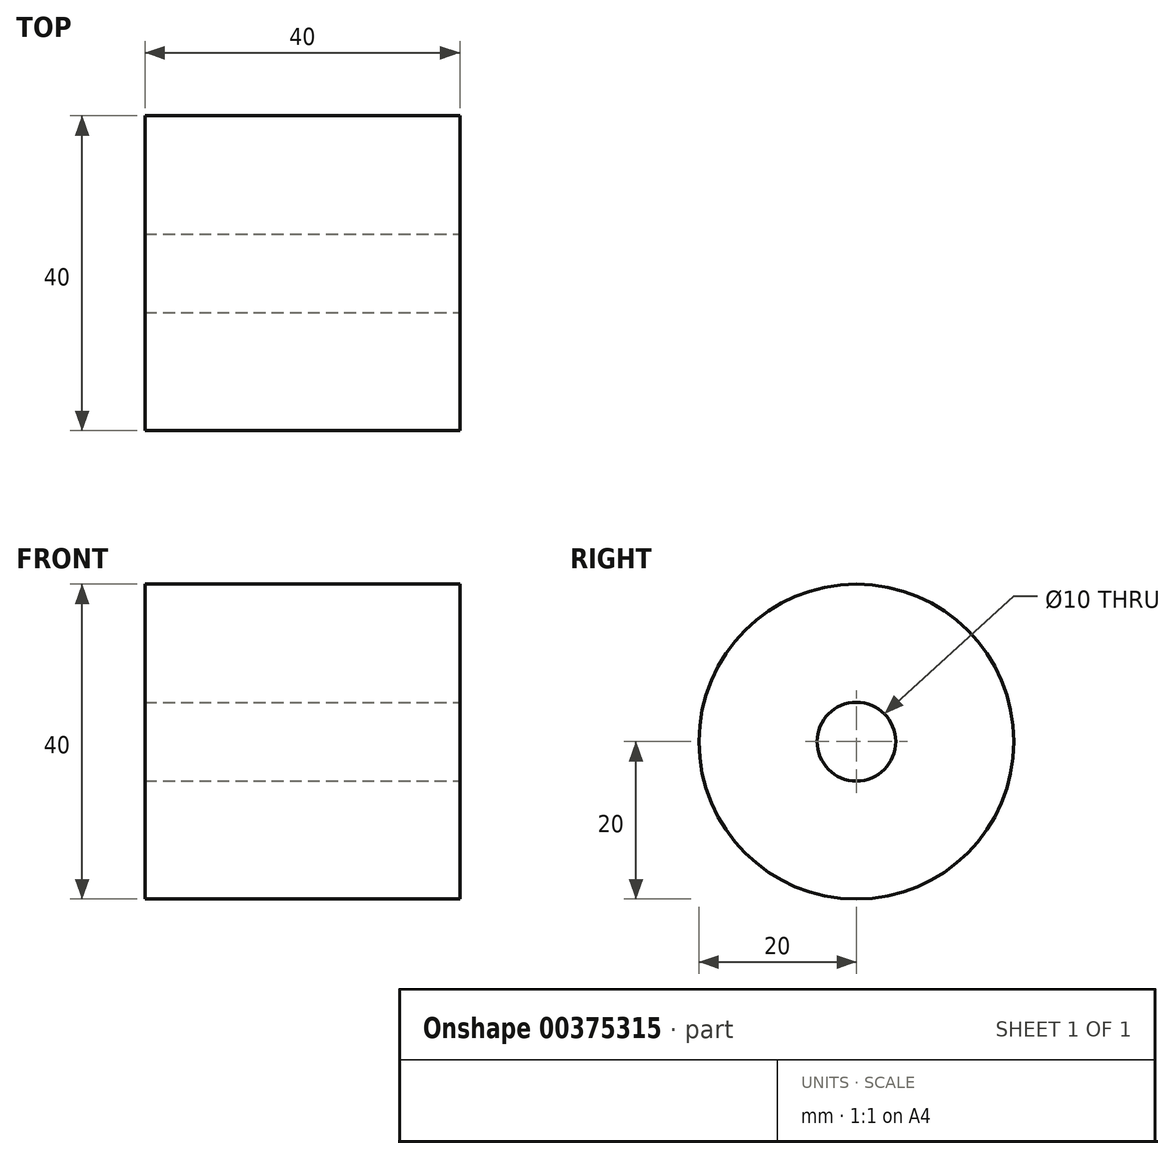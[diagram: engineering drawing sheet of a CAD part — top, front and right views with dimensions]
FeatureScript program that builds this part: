
annotation { "Feature Type Name" : "Feature", "Feature Type Description" : "" }
export const myFeature = defineFeature(function(context is Context, id is Id, definition is map)
    precondition{}
    {
        {
            var Q0;
            Q0=qCreatedBy(makeId("Front.planeOp"),FACE);
            var sketch = newSketch(context, id + "F0", { "sketchPlane" : qUnion([Q0])});
            skLineSegment(sketch, "E0.bottom", {"start": v(-20.03, 20) * mm, "end": v(19.97, 20) * mm});
            skLineSegment(sketch, "E0.top", {"start": v(-20.03, 0) * mm, "end": v(19.97, 0) * mm});
            skLineSegment(sketch, "E0.left", {"start": v(-20.03, 20) * mm, "end": v(-20.03, 0) * mm});
            skLineSegment(sketch, "E0.right", {"start": v(19.97, 20) * mm, "end": v(19.97, 0) * mm});
            skSolve(sketch);
        }
        {
            var Q0;
            Q0 = qSketchRegion(id + "F0", true);
            var Q1;
            Q1=sQuery(id+"F0.wireOp",EDGE,"E0.top");
            revolve(context, id + "F1", {"entities" : qUnion([Q0]), "axis" : qUnion([Q1]), "revolveType" : RevolveType.FULL});
        }
        {
            var Q0;
            Q0=makeQuery(id+"F1.opRevolve","SWEPT_FACE",FACE,{"disambiguationData":[OSD([sQuery(id+"F0.wireOp",EDGE,"E0.right")])]});
            var sketch = newSketch(context, id + "F2", { "sketchPlane" : qUnion([Q0])});
            skCircle(sketch, "E1", {"center": v(0, 0) * mm, "radius": 5 * mm});
            skSolve(sketch);
        }
        {
            var Q0;
            Q0 = qSketchRegion(id + "F2", true);
            extrude(context, id + "F3", {"entities" : qUnion([Q0]), "operationType" : NewBodyOperationType.REMOVE, "endBound" : BoundingType.THROUGH_ALL, "oppositeDirection" : true, "depth" : 25 * mm});
        }
    });
